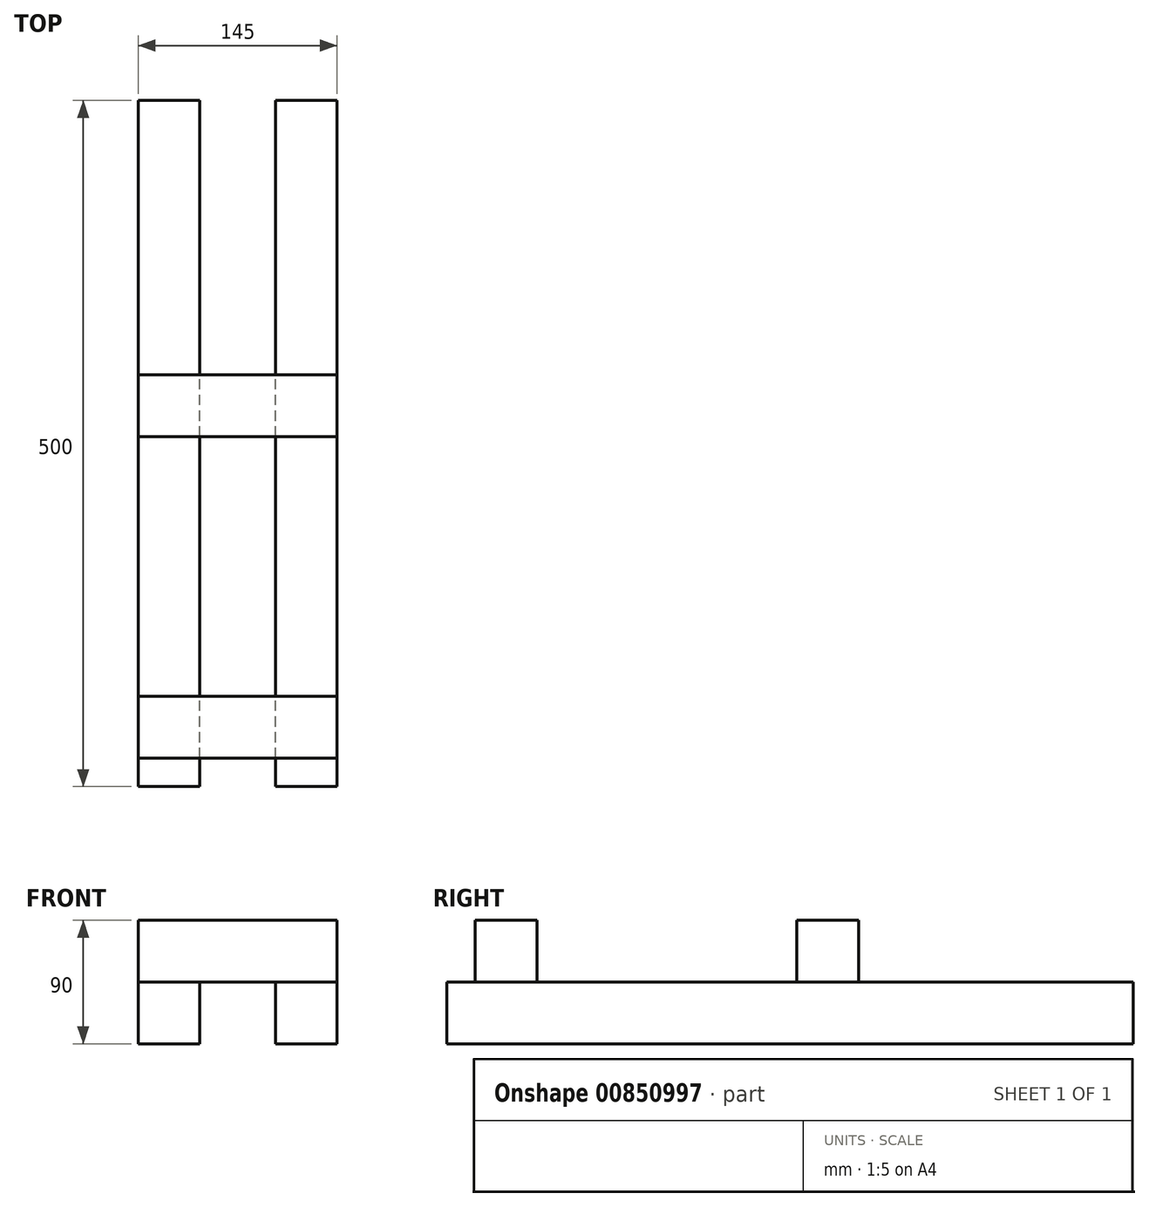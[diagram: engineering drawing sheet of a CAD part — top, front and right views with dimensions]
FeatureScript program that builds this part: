
annotation { "Feature Type Name" : "Feature", "Feature Type Description" : "" }
export const myFeature = defineFeature(function(context is Context, id is Id, definition is map)
    precondition{}
    {
        {
            var Q0;
            Q0=qCreatedBy(makeId("Front.planeOp"),FACE);
            var sketch = newSketch(context, id + "F0", { "sketchPlane" : qUnion([Q0])});
            skLineSegment(sketch, "E0.bottom", {"start": v(27.5, 22.5) * mm, "end": v(72.5, 22.5) * mm});
            skLineSegment(sketch, "E0.top", {"start": v(27.5, -22.5) * mm, "end": v(72.5, -22.5) * mm});
            skLineSegment(sketch, "E0.left", {"start": v(27.5, 22.5) * mm, "end": v(27.5, -22.5) * mm});
            skLineSegment(sketch, "E0.right", {"start": v(72.5, 22.5) * mm, "end": v(72.5, -22.5) * mm});
            skLineSegment(sketch, "E1.bottom", {"start": v(-72.5, 22.5) * mm, "end": v(-27.5, 22.5) * mm});
            skLineSegment(sketch, "E1.top", {"start": v(-72.5, -22.5) * mm, "end": v(-27.5, -22.5) * mm});
            skLineSegment(sketch, "E1.left", {"start": v(-72.5, 22.5) * mm, "end": v(-72.5, -22.5) * mm});
            skLineSegment(sketch, "E1.right", {"start": v(-27.5, 22.5) * mm, "end": v(-27.5, -22.5) * mm});
            skSolve(sketch);
        }
        {
            var Q0;
            Q0 = qSketchRegion(id + "F0", true);
            extrude(context, id + "F1", {"entities" : qUnion([Q0]), "depth" : 500 * mm, "offsetDistance" : 25 * mm});
        }
        {
            var Q0;
            Q0=makeQuery(id+"F1.opExtrude","SWEPT_FACE",FACE,{"disambiguationData":[OSD([sQuery(id+"F0.wireOp",EDGE,"E0.right")])]});
            var sketch = newSketch(context, id + "F2", { "sketchPlane" : qUnion([Q0])});
            skLineSegment(sketch, "E2.bottom", {"start": v(-200, 67.5) * mm, "end": v(-245, 67.5) * mm});
            skLineSegment(sketch, "E2.top", {"start": v(-200, 22.5) * mm, "end": v(-245, 22.5) * mm});
            skLineSegment(sketch, "E2.left", {"start": v(-200, 67.5) * mm, "end": v(-200, 22.5) * mm});
            skLineSegment(sketch, "E2.right", {"start": v(-245, 67.5) * mm, "end": v(-245, 22.5) * mm});
            skSolve(sketch);
        }
        {
            var Q0;
            Q0 = qSketchRegion(id + "F2", true);
            extrude(context, id + "F3", {"entities" : qUnion([Q0]), "oppositeDirection" : true, "depth" : 145 * mm, "offsetDistance" : 25 * mm});
        }
        {
            var Q0;
            Q0=makeQuery(id+"F1.opExtrude","SWEPT_FACE",FACE,{"disambiguationData":[OSD([sQuery(id+"F0.wireOp",EDGE,"E0.right")])]});
            var sketch = newSketch(context, id + "F4", { "sketchPlane" : qUnion([Q0])});
            skLineSegment(sketch, "E3.bottom", {"start": v(-434.37, 22.5) * mm, "end": v(-479.37, 22.5) * mm});
            skLineSegment(sketch, "E3.top", {"start": v(-434.37, 67.5) * mm, "end": v(-479.37, 67.5) * mm});
            skLineSegment(sketch, "E3.left", {"start": v(-434.37, 22.5) * mm, "end": v(-434.37, 67.5) * mm});
            skLineSegment(sketch, "E3.right", {"start": v(-479.37, 22.5) * mm, "end": v(-479.37, 67.5) * mm});
            skSolve(sketch);
        }
        {
            var Q0;
            Q0 = qSketchRegion(id + "F4", true);
            extrude(context, id + "F5", {"entities" : qUnion([Q0]), "oppositeDirection" : true, "depth" : 145 * mm, "offsetDistance" : 25 * mm});
        }
    });
